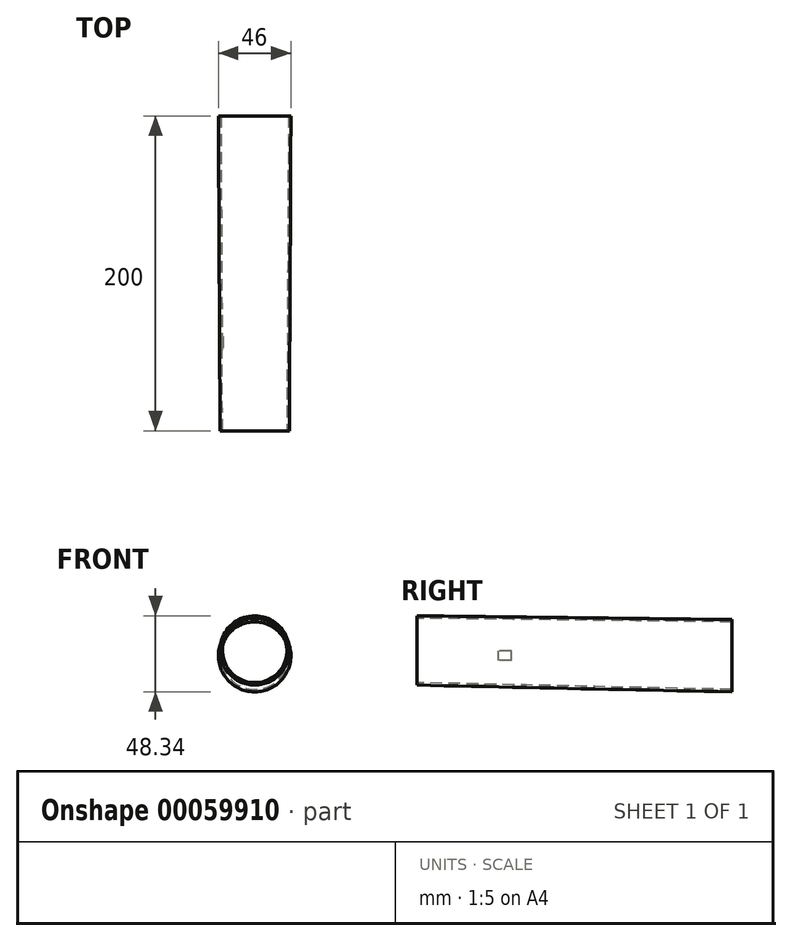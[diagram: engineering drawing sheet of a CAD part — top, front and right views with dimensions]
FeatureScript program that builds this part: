
annotation { "Feature Type Name" : "Feature", "Feature Type Description" : "" }
export const myFeature = defineFeature(function(context is Context, id is Id, definition is map)
    precondition{}
    {
        {
            var Q0;
            Q0=qCreatedBy(makeId("Front.planeOp"),FACE);
            var sketch = newSketch(context, id + "F0", { "sketchPlane" : qUnion([Q0])});
            skCircle(sketch, "E0", {"center": v(0, 0) * mm, "radius": 23 * mm});
            skSolve(sketch);
        }
        {
            var Q0;
            Q0=qCreatedBy(makeId("Front.planeOp"),FACE);
            cPlane(context, id + "F1", {"entities" : qUnion([Q0]), "cplaneType" : CPlaneType.OFFSET, "offset" : 200 * mm, "width" : 150 * mm, "height" : 150 * mm});
        }
        {
            var Q0;
            Q0=qCreatedBy(id+"F1.planeOp",FACE);
            var sketch = newSketch(context, id + "F2", { "sketchPlane" : qUnion([Q0])});
            skCircle(sketch, "E1", {"center": v(0, 3.34) * mm, "radius": 22 * mm});
            skSolve(sketch);
        }
        {
            var Q0;
            Q0 = qSketchRegion(id + "F0", true);
            var Q1;
            Q1 = qSketchRegion(id + "F2", true);
            loft(context, id + "F3", {"sheetProfilesArray" : [{ "sheetProfileEntities" : qUnion([Q0]) }, { "sheetProfileEntities" : qUnion([Q1]) }]});
        }
        {
            var Q0;
            Q0=makeQuery(id+"F3.opLoft","CAP_FACE",FACE,{"disambiguationData":[OSD([makeQuery(id+"F0.imprint","IMPRINT",FACE,{"disambiguationData":[TD([[makeQuery(id+"F0.imprint","IMPRINT",EDGE,{"derivedFrom":sQuery(id+"F0.wireOp",EDGE,"E0")}),1.0]])]})])],"isStart":true});
            var Q1;
            Q1=makeQuery(id+"F3.opLoft","CAP_FACE",FACE,{"disambiguationData":[OSD([makeQuery(id+"F2.imprint","IMPRINT",FACE,{"disambiguationData":[TD([[makeQuery(id+"F2.imprint","IMPRINT",EDGE,{"derivedFrom":sQuery(id+"F2.wireOp",EDGE,"E1")}),1.0]])]})])],"isStart":true});
            shell(context, id + "F4", {"entities" : qUnion([Q0, Q1]), "thickness" : 1.5 * mm});
        }
        {
            var Q0;
            Q0=qCreatedBy(makeId("Right.planeOp"),FACE);
            var sketch = newSketch(context, id + "F5", { "sketchPlane" : qUnion([Q0])});
            skLineSegment(sketch, "E2.bottom", {"start": v(-148, 3) * mm, "end": v(-140, 3) * mm});
            skLineSegment(sketch, "E2.top", {"start": v(-148, -3) * mm, "end": v(-140, -3) * mm});
            skLineSegment(sketch, "E2.left", {"start": v(-148, 3) * mm, "end": v(-148, -3) * mm});
            skLineSegment(sketch, "E2.right", {"start": v(-140, 3) * mm, "end": v(-140, -3) * mm});
            skPoint(sketch, "E2.middle", {"position": v(-144, 0) * mm});
            skSolve(sketch);
        }
        {
            var Q0;
            Q0 = qSketchRegion(id + "F5", true);
            extrude(context, id + "F6", {"entities" : qUnion([Q0]), "operationType" : NewBodyOperationType.REMOVE, "oppositeDirection" : true, "depth" : 30 * mm});
        }
    });
